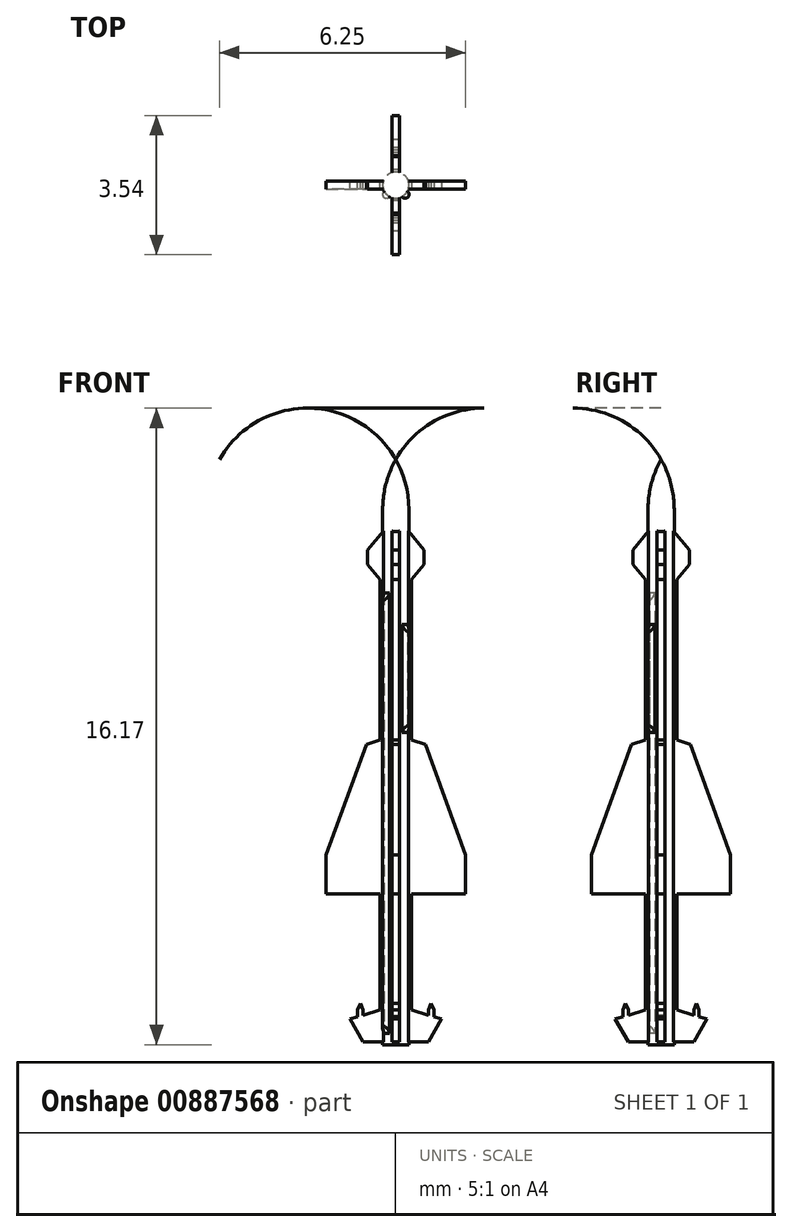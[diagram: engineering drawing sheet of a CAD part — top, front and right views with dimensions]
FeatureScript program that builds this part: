
annotation { "Feature Type Name" : "Feature", "Feature Type Description" : "" }
export const myFeature = defineFeature(function(context is Context, id is Id, definition is map)
    precondition{}
    {
        {
            assignVariable(context, id + "F0", {"name" : "Scale", "anyValue" : 300});
        }
        {
            var Q0;
            Q0=qCreatedBy(makeId("Front.planeOp"),FACE);
            var sketch = newSketch(context, id + "F1", { "sketchPlane" : qUnion([Q0])});
            skLineSegment(sketch, "E0", {"start": v(0, 0) * mm, "end": v(0, 14.87) * mm});
            skLineSegment(sketch, "E1", {"start": v(0.33, 13.6) * mm, "end": v(0.33, 0) * mm});
            skLineSegment(sketch, "E2", {"start": v(0.33, 0) * mm, "end": v(0, 0) * mm});
            skArc(sketch, "E3", {"start": v(0.33, 13.6) * mm, "mid": v(0.25, 14.25) * mm, "end": v(0, 14.87) * mm});
            skSolve(sketch);
        }
        {
            var Q0;
            Q0=makeQuery(id+"F1.imprint","IMPRINT",FACE,{"disambiguationData":[TD([[makeQuery(id+"F1.imprint","IMPRINT",EDGE,{"derivedFrom":sQuery(id+"F1.wireOp",EDGE,"E0")}),-1.0]])]});
            var Q1;
            Q1=sQuery(id+"F1.wireOp",EDGE,"E0");
            revolve(context, id + "F2", {"surfaceOperationType" : NewSurfaceOperationType.NEW, "entities" : qUnion([Q0]), "axis" : qUnion([Q1]), "revolveType" : RevolveType.FULL});
        }
        {
            var Q0;
            Q0=qCreatedBy(makeId("Front.planeOp"),FACE);
            var sketch = newSketch(context, id + "F3", { "sketchPlane" : qUnion([Q0])});
            skLineSegment(sketch, "E4.0", {"start": v(0.33, 13.6) * mm, "end": v(-0.33, 13.6) * mm, "construction": true});
            skLineSegment(sketch, "E5", {"start": v(0, 0.07) * mm, "end": v(0.83, 0.07) * mm});
            skLineSegment(sketch, "E6", {"start": v(1.17, 0.65) * mm, "end": v(0.33, 0.9) * mm});
            skLineSegment(sketch, "E7", {"start": v(0.4, 0.88) * mm, "end": v(0.4, 3.83) * mm});
            skLineSegment(sketch, "E8", {"start": v(0.4, 3.83) * mm, "end": v(1.77, 3.83) * mm});
            skLineSegment(sketch, "E9", {"start": v(0, 13.44) * mm, "end": v(0, 0.07) * mm});
            skLineSegment(sketch, "E10", {"start": v(0.33, 13.6) * mm, "end": v(0.33, 0) * mm, "construction": true});
            skLineSegment(sketch, "E11", {"start": v(0.4, 0.88) * mm, "end": v(0.33, 0.9) * mm});
            skLineSegment(sketch, "E12", {"start": v(0.83, 0.07) * mm, "end": v(1.17, 0.65) * mm});
            skLineSegment(sketch, "E13", {"start": v(1.77, 3.83) * mm, "end": v(1.77, 4.82) * mm});
            skLineSegment(sketch, "E14", {"start": v(0.4, 7.75) * mm, "end": v(0.4, 11.81) * mm});
            skLineSegment(sketch, "E15", {"start": v(0.72, 12.2) * mm, "end": v(0.4, 11.81) * mm});
            skLineSegment(sketch, "E16", {"start": v(0.72, 12.2) * mm, "end": v(0.72, 12.57) * mm});
            skLineSegment(sketch, "E17", {"start": v(0.72, 12.57) * mm, "end": v(0, 13.44) * mm});
            skLineSegment(sketch, "E18", {"start": v(0.83, 0.75) * mm, "end": v(0.83, 0.89) * mm});
            skLineSegment(sketch, "E19", {"start": v(0.83, 0.89) * mm, "end": v(0.9, 1.05) * mm});
            skLineSegment(sketch, "E20", {"start": v(0.9, 1.05) * mm, "end": v(0.97, 0.89) * mm});
            skLineSegment(sketch, "E21", {"start": v(0.97, 0.89) * mm, "end": v(0.97, 0.71) * mm});
            skLineSegment(sketch, "E22", {"start": v(1.77, 4.82) * mm, "end": v(0.75, 7.63) * mm});
            skLineSegment(sketch, "E23", {"start": v(0.75, 7.63) * mm, "end": v(0.4, 7.75) * mm});
            skPoint(sketch, "E24", {"position": v(0.33, 7.77) * mm});
            skPoint(sketch, "E25", {"position": v(0.33, 11.73) * mm});
            skPoint(sketch, "E26", {"position": v(0.33, 13.03) * mm});
            skSolve(sketch);
        }
        {
            var Q0;
            Q0=qSketchRegion(id+"F3",true);
            extrude(context, id + "F4", {"entities" : qUnion([Q0]), "operationType" : NewBodyOperationType.ADD, "oppositeDirection" : true, "depth" : .2 * mm, "offsetDistance" : 25 * mm, "symmetric" : true});
        }
        {
            var Q0;
            Q0=makeQuery(id+"F2.opRevolve","SWEPT_BODY",BODY,{"disambiguationData":[OSD([sQuery(id+"F1.wireOp",EDGE,"E0"),sQuery(id+"F1.wireOp",EDGE,"E1"),sQuery(id+"F1.wireOp",EDGE,"E2"),sQuery(id+"F1.wireOp",EDGE,"h1jDSi8t-veb7-85qg-XgDk-6E8DmZjBuz4r")])]});
            var Q1;
            Q1=makeQuery(id+"F2.opRevolve","SWEPT_FACE",FACE,{"disambiguationData":[OSD([sQuery(id+"F1.wireOp",EDGE,"E1")])]});
            circularPattern(context, id + "F5", {"operationType" : NewBodyOperationType.ADD, "entities" : qUnion([Q0]), "axis" : qUnion([Q1]), "angle" : 360 * degree, "instanceCount" : 4, "equalSpace" : true, "computeTransformsWithoutBuiltin" : true});
        }
        {
            var Q0;
            Q0=qCreatedBy(makeId("Top.planeOp"),FACE);
            cPlane(context, id + "F6", {"entities" : qUnion([Q0]), "cplaneType" : CPlaneType.OFFSET, "offset" : (140 / getVariable(context, 'Scale')) * mm, "width" : 150 * mm, "height" : 150 * mm});
        }
        {
            var Q0;
            Q0=qCreatedBy(id+"F6.planeOp",FACE);
            var sketch = newSketch(context, id + "F7", { "sketchPlane" : qUnion([Q0])});
            skLineSegment(sketch, "E27", {"start": v(-0.3, -0.16) * mm, "end": v(-0.11, 0.03) * mm});
            skLineSegment(sketch, "E28", {"start": v(-0.11, 0.03) * mm, "end": v(0.03, -0.11) * mm});
            skLineSegment(sketch, "E29", {"start": v(0.03, -0.11) * mm, "end": v(-0.16, -0.3) * mm});
            skArc(sketch, "E30", {"start": v(-0.3, -0.16) * mm, "mid": v(-0.3, -0.3) * mm, "end": v(-0.16, -0.3) * mm});
            skLineSegment(sketch, "E31", {"start": v(-0.04, -0.04) * mm, "end": v(0, 0) * mm, "construction": true});
            skLineSegment(sketch, "E32", {"start": v(0, 0) * mm, "end": v(-0.48, 0) * mm, "construction": true});
            skSolve(sketch);
        }
        {
            var Q0;
            Q0=makeQuery(id+"F7.imprint","IMPRINT",FACE,{"disambiguationData":[TD([[makeQuery(id+"F7.imprint","IMPRINT",EDGE,{"derivedFrom":sQuery(id+"F7.wireOp",EDGE,"E27")}),-1.0]])]});
            extrude(context, id + "F8", {"entities" : qUnion([Q0]), "operationType" : NewBodyOperationType.ADD, "depth" : (3250 / getVariable(context, 'Scale')) * mm, "offsetDistance" : 25 * mm});
        }
        {
            var Q0;
            Q0=qCreatedBy(makeId("Top.planeOp"),FACE);
            cPlane(context, id + "F9", {"entities" : qUnion([Q0]), "cplaneType" : CPlaneType.OFFSET, "offset" : (2430 / getVariable(context, 'Scale')) * mm, "width" : 150 * mm, "height" : 150 * mm});
        }
        {
            var Q0;
            Q0=qCreatedBy(id+"F9.planeOp",FACE);
            var sketch = newSketch(context, id + "F10", { "sketchPlane" : qUnion([Q0])});
            skLineSegment(sketch, "E33", {"start": v(0.03, -0.17) * mm, "end": v(0.17, -0.03) * mm});
            skLineSegment(sketch, "E34", {"start": v(0.17, -0.03) * mm, "end": v(0.3, -0.16) * mm});
            skLineSegment(sketch, "E35", {"start": v(0.16, -0.3) * mm, "end": v(0.03, -0.17) * mm});
            skArc(sketch, "E36", {"start": v(0.16, -0.3) * mm, "mid": v(0.3, -0.3) * mm, "end": v(0.3, -0.16) * mm});
            skLineSegment(sketch, "E37", {"start": v(0, -0.58) * mm, "end": v(0, 0) * mm, "construction": true});
            skLineSegment(sketch, "E38", {"start": v(0, 0) * mm, "end": v(0.1, -0.1) * mm, "construction": true});
            skSolve(sketch);
        }
        {
            var Q0;
            Q0=qSketchRegion(id+"F10",true);
            extrude(context, id + "F11", {"entities" : qUnion([Q0]), "operationType" : NewBodyOperationType.ADD, "depth" : (720 / getVariable(context, 'Scale')) * mm, "offsetDistance" : 25 * mm});
        }
        {
            var Q0;
            Q0=makeQuery(id+"F8.boolean.opBoolean","INTERSECT",EDGE,{"derivedFrom":[makeQuery(id+"F2.opRevolve","SWEPT_FACE",FACE,{"disambiguationData":[OSD([sQuery(id+"F1.wireOp",EDGE,"E1")])]}),makeQuery(id+"F8.opExtrude","CAP_FACE",FACE,{"disambiguationData":[OSD([sQuery(id+"F7.wireOp",EDGE,"E27"),sQuery(id+"F7.wireOp",EDGE,"E28"),sQuery(id+"F7.wireOp",EDGE,"E29"),sQuery(id+"F7.wireOp",EDGE,"E30")])],"isStart":false})]});
            var Q1;
            Q1=makeQuery(id+"F8.boolean.opBoolean","INTERSECT",EDGE,{"derivedFrom":[makeQuery(id+"F2.opRevolve","SWEPT_FACE",FACE,{"disambiguationData":[OSD([sQuery(id+"F1.wireOp",EDGE,"E1")])]}),makeQuery(id+"F8.opExtrude","CAP_FACE",FACE,{"disambiguationData":[OSD([sQuery(id+"F7.wireOp",EDGE,"E27"),sQuery(id+"F7.wireOp",EDGE,"E28"),sQuery(id+"F7.wireOp",EDGE,"E29"),sQuery(id+"F7.wireOp",EDGE,"E30")])],"isStart":true})]});
            var Q2;
            Q2=makeQuery(id+"F11.boolean.opBoolean","INTERSECT",EDGE,{"derivedFrom":[makeQuery(id+"F2.opRevolve","SWEPT_FACE",FACE,{"disambiguationData":[OSD([sQuery(id+"F1.wireOp",EDGE,"E1")])]}),makeQuery(id+"F11.opExtrude","CAP_FACE",FACE,{"disambiguationData":[OSD([sQuery(id+"F10.wireOp",EDGE,"E33"),sQuery(id+"F10.wireOp",EDGE,"E34"),sQuery(id+"F10.wireOp",EDGE,"E35"),sQuery(id+"F10.wireOp",EDGE,"E36")])],"isStart":true})]});
            var Q3;
            Q3=makeQuery(id+"F11.boolean.opBoolean","INTERSECT",EDGE,{"derivedFrom":[makeQuery(id+"F2.opRevolve","SWEPT_FACE",FACE,{"disambiguationData":[OSD([sQuery(id+"F1.wireOp",EDGE,"E1")])]}),makeQuery(id+"F11.opExtrude","CAP_FACE",FACE,{"disambiguationData":[OSD([sQuery(id+"F10.wireOp",EDGE,"E33"),sQuery(id+"F10.wireOp",EDGE,"E34"),sQuery(id+"F10.wireOp",EDGE,"E35"),sQuery(id+"F10.wireOp",EDGE,"E36")])],"isStart":false})]});
            chamfer(context, id + "F12", {"entities" : qUnion([Q0, Q1, Q2, Q3]), "chamferType" : ChamferType.OFFSET_ANGLE, "width" : .1 * mm, "oppositeDirection" : true, "angle" : 60 * degree, "tangentPropagation" : true});
        }
    });
